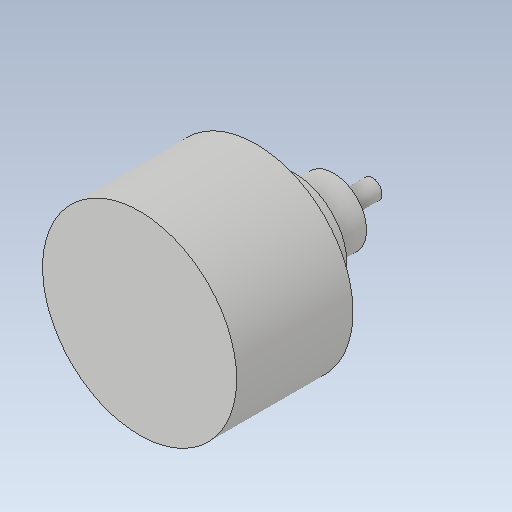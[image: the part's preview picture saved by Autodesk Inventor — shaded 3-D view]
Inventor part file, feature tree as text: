
AUTODESK INVENTOR PART (.ipt)
format: ipt  version: 2020 (Build 240168000, 168)  size: 113,664 bytes
history: native  units: mm
features: other x4, extrude x4, sketch x4, reference x1
ambient origin geometry x8: Origin, YZ Plane, XZ Plane, XY Plane, X Axis, Y Axis, Z Axis, Center Point
bodies: Body1 (feature_tree)
feature tree (13):
  other  "Твердое тело1"
  extrude  "Выдавливание1"  Depth=50.0mm
  extrude  "Выдавливание2"  Depth=30.0mm TaperAngle=0.0deg
  extrude  "Выдавливание3"  Depth=10.0mm TaperAngle=0.0deg
  extrude  "Выдавливание4"  Depth=17.0mm
  sketch  "Эскиз1"
  sketch  "Эскиз2"
  reference  "Ссылка2"
  sketch  "Эскиз3"
  sketch  "Эскиз4"
  other  "<userpath>\GoogleDrive\My_project\Механика\Фотоштатив\Сборка1.iam"
  other  "Сборка1.iam"
  other  "Гор. шарнир:1"
